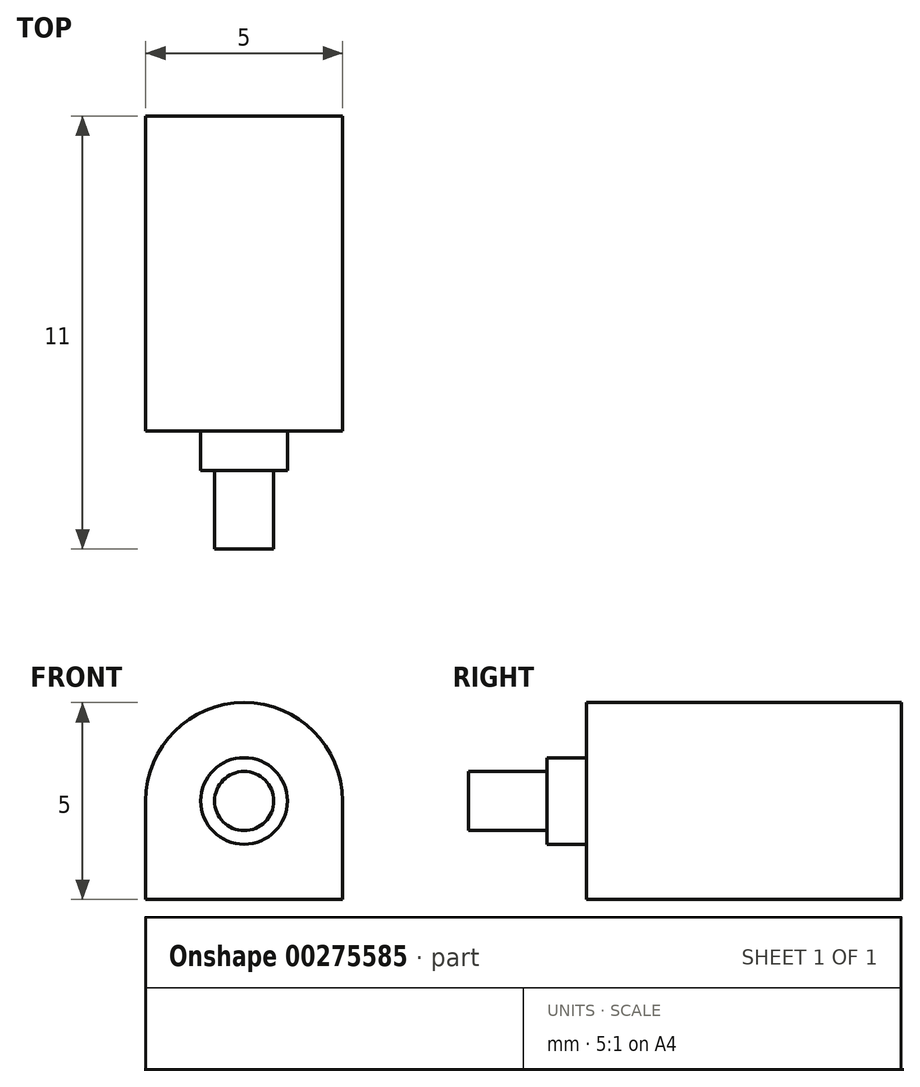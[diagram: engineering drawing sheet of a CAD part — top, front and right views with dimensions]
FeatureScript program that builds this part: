
annotation { "Feature Type Name" : "Feature", "Feature Type Description" : "" }
export const myFeature = defineFeature(function(context is Context, id is Id, definition is map)
    precondition{}
    {
        {
            var Q0;
            Q0=qCreatedBy(makeId("Front.planeOp"),FACE);
            var sketch = newSketch(context, id + "F0", { "sketchPlane" : qUnion([Q0])});
            skArc(sketch, "E0", {"start": v(-2.5, 0) * mm, "mid": v(0, 2.5) * mm, "end": v(2.5, 0) * mm});
            skLineSegment(sketch, "E1", {"start": v(-2.5, 0) * mm, "end": v(-2.5, -2.5) * mm});
            skLineSegment(sketch, "E2", {"start": v(-2.5, -2.5) * mm, "end": v(2.5, -2.5) * mm});
            skLineSegment(sketch, "E3", {"start": v(2.5, -2.5) * mm, "end": v(2.5, 0) * mm});
            skSolve(sketch);
        }
        {
            var Q0;
            Q0 = qSketchRegion(id + "F0", true);
            extrude(context, id + "F1", {"entities" : qUnion([Q0]), "depth" : 8 * mm});
        }
        {
            var Q0;
            Q0=makeQuery(id+"F1.opExtrude","CAP_FACE",FACE,{"disambiguationData":[OSD([sQuery(id+"F0.wireOp",EDGE,"E0"),sQuery(id+"F0.wireOp",EDGE,"E1"),sQuery(id+"F0.wireOp",EDGE,"E2"),sQuery(id+"F0.wireOp",EDGE,"E3")])],"isStart":false});
            var sketch = newSketch(context, id + "F2", { "sketchPlane" : qUnion([Q0])});
            skCircle(sketch, "E4", {"center": v(0, 0) * mm, "radius": 1.1 * mm});
            skSolve(sketch);
        }
        {
            var Q0;
            Q0 = qSketchRegion(id + "F2", true);
            extrude(context, id + "F3", {"entities" : qUnion([Q0]), "operationType" : NewBodyOperationType.ADD, "depth" : 1 * mm});
        }
        {
            var Q0;
            Q0=makeQuery(id+"F3.opExtrude","CAP_FACE",FACE,{"disambiguationData":[OSD([sQuery(id+"F2.wireOp",EDGE,"E4")])],"isStart":false});
            var sketch = newSketch(context, id + "F4", { "sketchPlane" : qUnion([Q0])});
            skCircle(sketch, "E5", {"center": v(0, 0) * mm, "radius": 0.75 * mm});
            skSolve(sketch);
        }
        {
            var Q0;
            Q0 = qSketchRegion(id + "F4", true);
            extrude(context, id + "F5", {"entities" : qUnion([Q0]), "operationType" : NewBodyOperationType.ADD, "depth" : 2 * mm});
        }
    });
